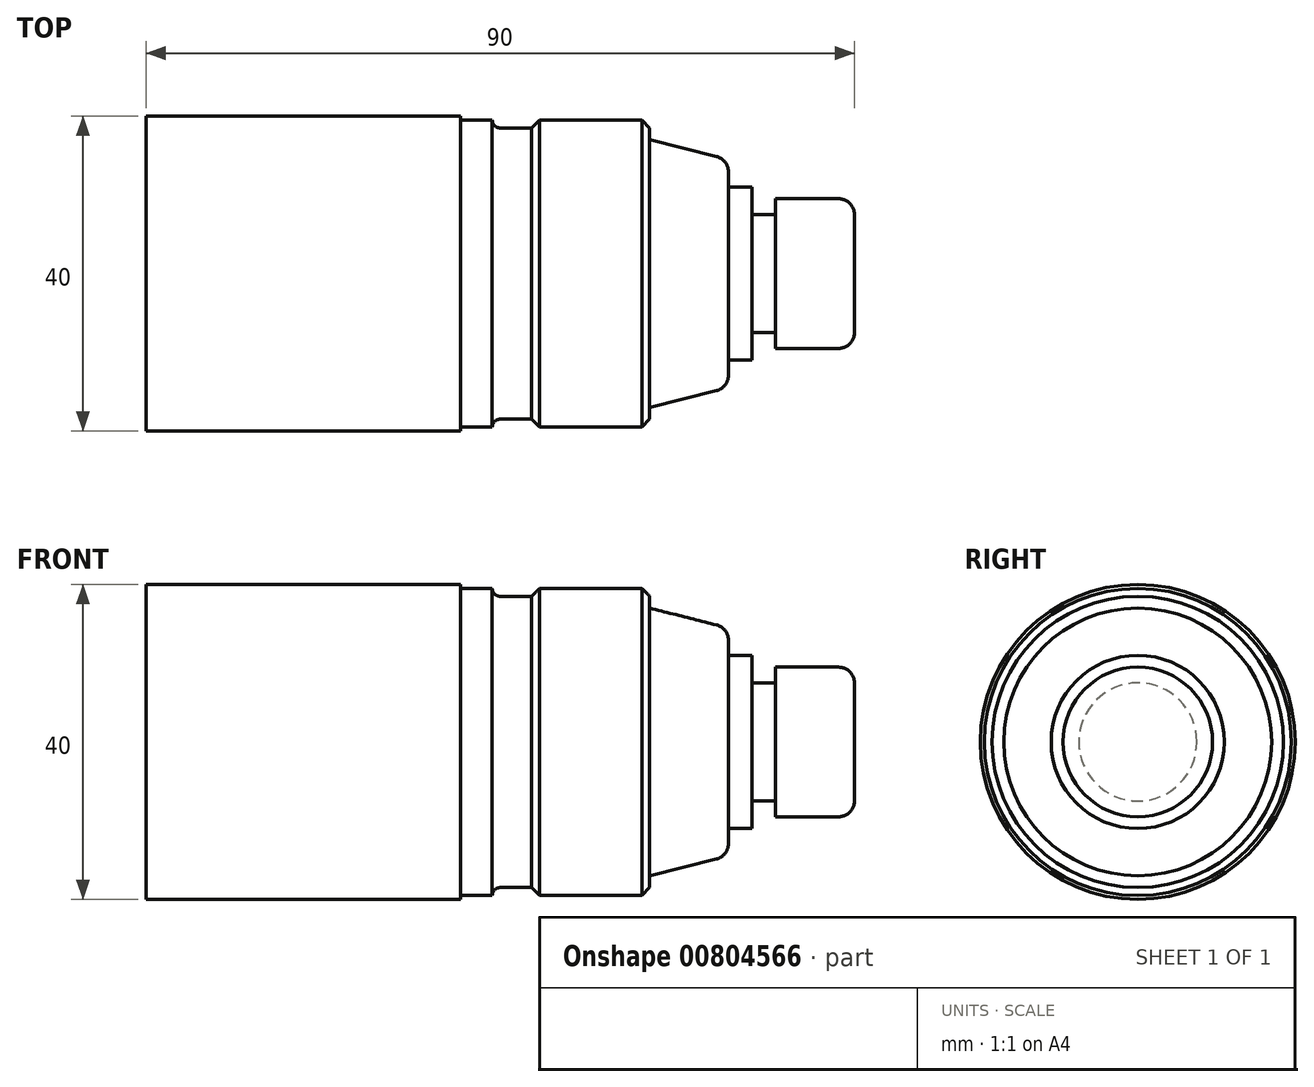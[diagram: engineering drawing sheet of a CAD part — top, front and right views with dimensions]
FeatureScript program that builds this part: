
annotation { "Feature Type Name" : "Feature", "Feature Type Description" : "" }
export const myFeature = defineFeature(function(context is Context, id is Id, definition is map)
    precondition{}
    {
        {
            var Q0;
            Q0=qCreatedBy(makeId("Front.planeOp"),FACE);
            var sketch = newSketch(context, id + "F0", { "sketchPlane" : qUnion([Q0])});
            skLineSegment(sketch, "E0", {"start": v(-80.11, 0) * mm, "end": v(-80.11, 20) * mm});
            skLineSegment(sketch, "E1", {"start": v(-80.11, 20) * mm, "end": v(-40.11, 20) * mm});
            skLineSegment(sketch, "E2", {"start": v(-40.11, 20) * mm, "end": v(-40.11, 19.5) * mm});
            skLineSegment(sketch, "E3", {"start": v(-40.11, 19.5) * mm, "end": v(-36.11, 19.5) * mm});
            skLineSegment(sketch, "E4", {"start": v(-36.11, 19.5) * mm, "end": v(-36.11, 19.5) * mm});
            skLineSegment(sketch, "E5", {"start": v(-35.11, 18.5) * mm, "end": v(-31.11, 18.5) * mm});
            skLineSegment(sketch, "E6", {"start": v(-31.11, 18.5) * mm, "end": v(-30.11, 19.5) * mm});
            skLineSegment(sketch, "E7", {"start": v(-30.11, 19.5) * mm, "end": v(-17.11, 19.5) * mm});
            skLineSegment(sketch, "E8", {"start": v(-17.11, 19.5) * mm, "end": v(-16.11, 18.5) * mm});
            skLineSegment(sketch, "E9", {"start": v(-16.11, 18.5) * mm, "end": v(-16.11, 17) * mm});
            skLineSegment(sketch, "E10", {"start": v(-6.11, 12.34) * mm, "end": v(-6.11, 11) * mm});
            skLineSegment(sketch, "E11", {"start": v(-6.11, 11) * mm, "end": v(-3.11, 11) * mm});
            skLineSegment(sketch, "E12", {"start": v(-3.11, 11) * mm, "end": v(-3.11, 7.5) * mm});
            skLineSegment(sketch, "E13", {"start": v(-3.11, 7.5) * mm, "end": v(-0.11, 7.5) * mm});
            skLineSegment(sketch, "E14", {"start": v(-0.11, 7.5) * mm, "end": v(-0.11, 9.5) * mm});
            skLineSegment(sketch, "E15", {"start": v(-0.11, 9.5) * mm, "end": v(7.89, 9.5) * mm});
            skLineSegment(sketch, "E16", {"start": v(9.89, 7.5) * mm, "end": v(9.89, 0) * mm});
            skPoint(sketch, "E17.visualSharp", {"position": v(-36.11, 18.5) * mm});
            skArc(sketch, "E17.filletArc", {"start": v(-36.11, 19.5) * mm, "mid": v(-35.82, 18.8) * mm, "end": v(-35.11, 18.5) * mm});
            skPoint(sketch, "E18.visualSharp", {"position": v(9.89, 9.5) * mm});
            skArc(sketch, "E18.filletArc", {"start": v(9.89, 7.5) * mm, "mid": v(9.3, 8.91) * mm, "end": v(7.89, 9.5) * mm});
            skLineSegment(sketch, "E19", {"start": v(-80.11, 0) * mm, "end": v(9.89, 0) * mm});
            skLineSegment(sketch, "E20", {"start": v(-6.11, 12.34) * mm, "end": v(-6.11, 12.92) * mm});
            skLineSegment(sketch, "E21", {"start": v(-7.62, 14.86) * mm, "end": v(-16.11, 17) * mm});
            skPoint(sketch, "E22.visualSharp", {"position": v(-6.11, 14.48) * mm});
            skArc(sketch, "E22.filletArc", {"start": v(-6.11, 12.92) * mm, "mid": v(-6.53, 14.15) * mm, "end": v(-7.62, 14.86) * mm});
            skSolve(sketch);
        }
        {
            var Q0;
            Q0=makeQuery(id+"F0.imprint","IMPRINT",FACE,{"disambiguationData":[TD([[makeQuery(id+"F0.imprint","IMPRINT",EDGE,{"derivedFrom":sQuery(id+"F0.wireOp",EDGE,"E0")}),-1.0]])]});
            var Q1;
            Q1=sQuery(id+"F0.wireOp",EDGE,"E19");
            revolve(context, id + "F1", {"surfaceOperationType" : NewSurfaceOperationType.NEW, "entities" : qUnion([Q0]), "axis" : qUnion([Q1]), "revolveType" : RevolveType.FULL});
        }
    });
